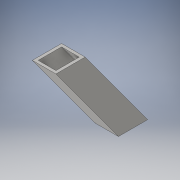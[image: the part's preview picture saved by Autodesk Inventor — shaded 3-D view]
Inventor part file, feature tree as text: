
AUTODESK INVENTOR PART (.ipt)
format: ipt  version: 2016 (Build 200138000, 138)  size: 108,544 bytes
history: native  units: in
note: dims shown in document units (in); Inventor stores cm internally (conversion verified against a paired STEP export)
features: sketch x3, extrude x1, sweep x1
ambient origin geometry x8: Origin, YZ Plane, XZ Plane, XY Plane, X Axis, Y Axis, Z Axis, Center Point
bodies: Solid1 (feature_tree)
feature tree (5):
  extrude  "Extrusion1"  Depth=1.0in
  sweep  "Sweep2"
  sketch  "Sketch1"  dims[d0=0.3697in d2=1.0in]
  sketch  "Sketch3"  dims[d3=3.625in d4=1.0in d5=0.0in d10=0.75in d12=0.125in d13=0.125in d16=0.125in d17=0.0in d18=0.0in]
  sketch  "3D Sketch1"
